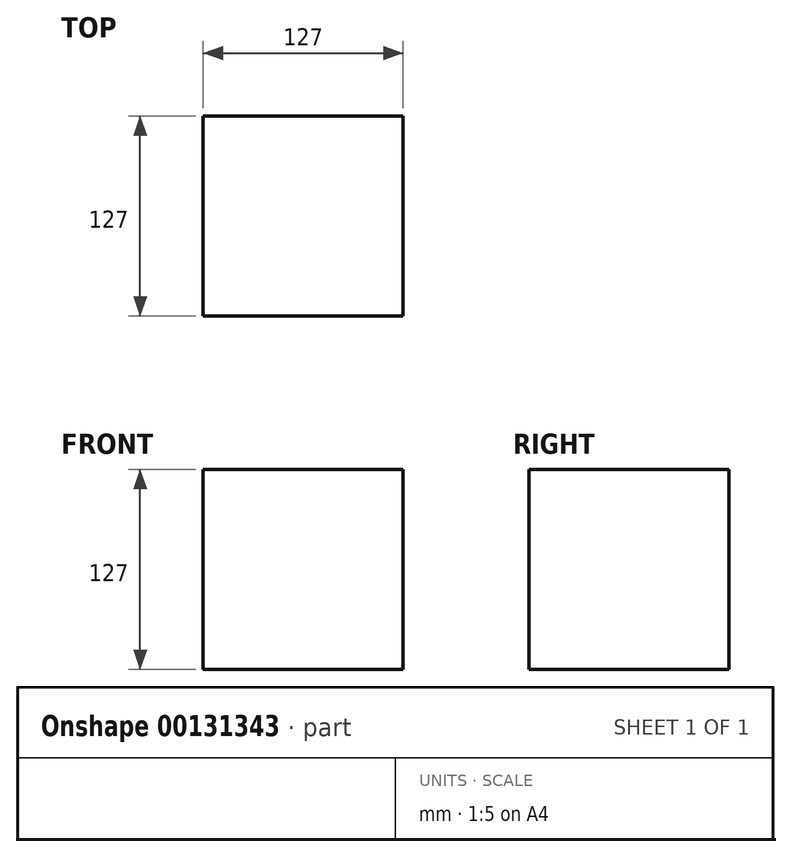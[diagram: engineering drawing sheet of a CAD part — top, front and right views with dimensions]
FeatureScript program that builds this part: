
annotation { "Feature Type Name" : "Feature", "Feature Type Description" : "" }
export const myFeature = defineFeature(function(context is Context, id is Id, definition is map)
    precondition{}
    {
        {
            var Q0;
            Q0=qCreatedBy(makeId("Front.planeOp"),FACE);
            var sketch = newSketch(context, id + "F0", { "sketchPlane" : qUnion([Q0])});
            skLineSegment(sketch, "E0.bottom", {"start": v(-69.16, 68.68) * mm, "end": v(57.84, 68.68) * mm});
            skLineSegment(sketch, "E0.top", {"start": v(-69.16, -58.32) * mm, "end": v(57.84, -58.32) * mm});
            skLineSegment(sketch, "E0.left", {"start": v(-69.16, 68.68) * mm, "end": v(-69.16, -58.32) * mm});
            skLineSegment(sketch, "E0.right", {"start": v(57.84, 68.68) * mm, "end": v(57.84, -58.32) * mm});
            skSolve(sketch);
        }
        {
            var Q0;
            Q0 = qSketchRegion(id + "F0", true);
            extrude(context, id + "F1", {"entities" : qUnion([Q0]), "depth" : 127 * mm});
        }
    });
